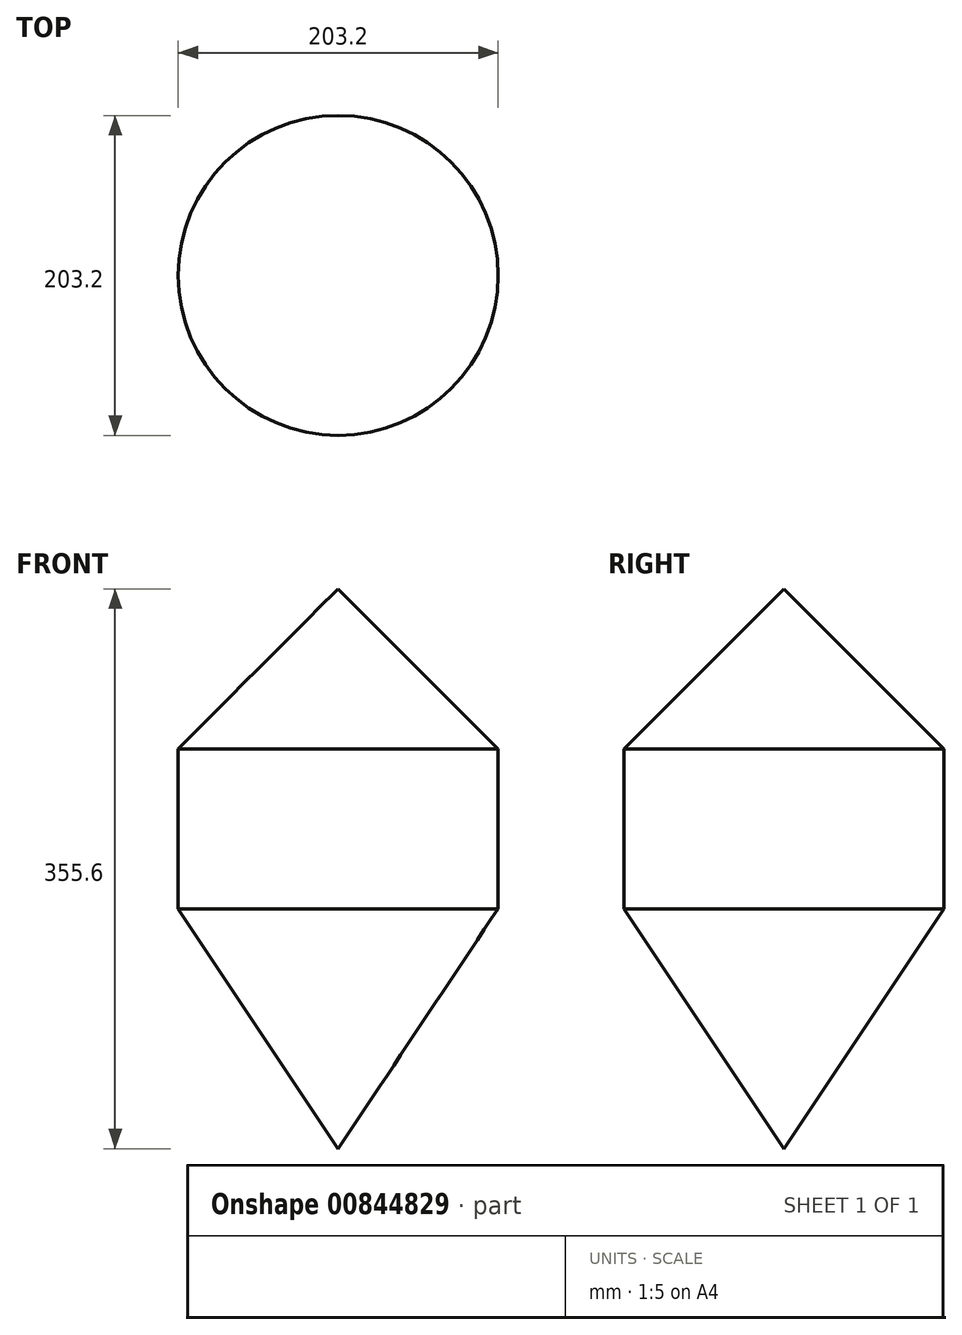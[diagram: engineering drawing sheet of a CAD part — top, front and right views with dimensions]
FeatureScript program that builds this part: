
annotation { "Feature Type Name" : "Feature", "Feature Type Description" : "" }
export const myFeature = defineFeature(function(context is Context, id is Id, definition is map)
    precondition{}
    {
        {
            var Q0;
            Q0=qCreatedBy(makeId("Front.planeOp"),FACE);
            var sketch = newSketch(context, id + "F0", { "sketchPlane" : qUnion([Q0])});
            skLineSegment(sketch, "E0", {"start": v(0, 502.39) * mm, "end": v(0, 146.79) * mm});
            skLineSegment(sketch, "E1", {"start": v(0, 146.79) * mm, "end": v(101.6, 299.19) * mm});
            skLineSegment(sketch, "E2", {"start": v(101.6, 299.19) * mm, "end": v(101.6, 400.79) * mm});
            skLineSegment(sketch, "E3", {"start": v(0, 502.39) * mm, "end": v(101.6, 400.79) * mm});
            skSolve(sketch);
        }
        {
            var Q0;
            Q0=makeQuery(id+"F0.imprint","IMPRINT",FACE,{"disambiguationData":[TD([[makeQuery(id+"F0.imprint","IMPRINT",EDGE,{"derivedFrom":sQuery(id+"F0.wireOp",EDGE,"E0")}),1.0]])]});
            var Q1;
            Q1=sQuery(id+"F0.wireOp",EDGE,"E0");
            revolve(context, id + "F1", {"surfaceOperationType" : NewSurfaceOperationType.NEW, "entities" : qUnion([Q0]), "axis" : qUnion([Q1]), "revolveType" : RevolveType.FULL});
        }
    });
